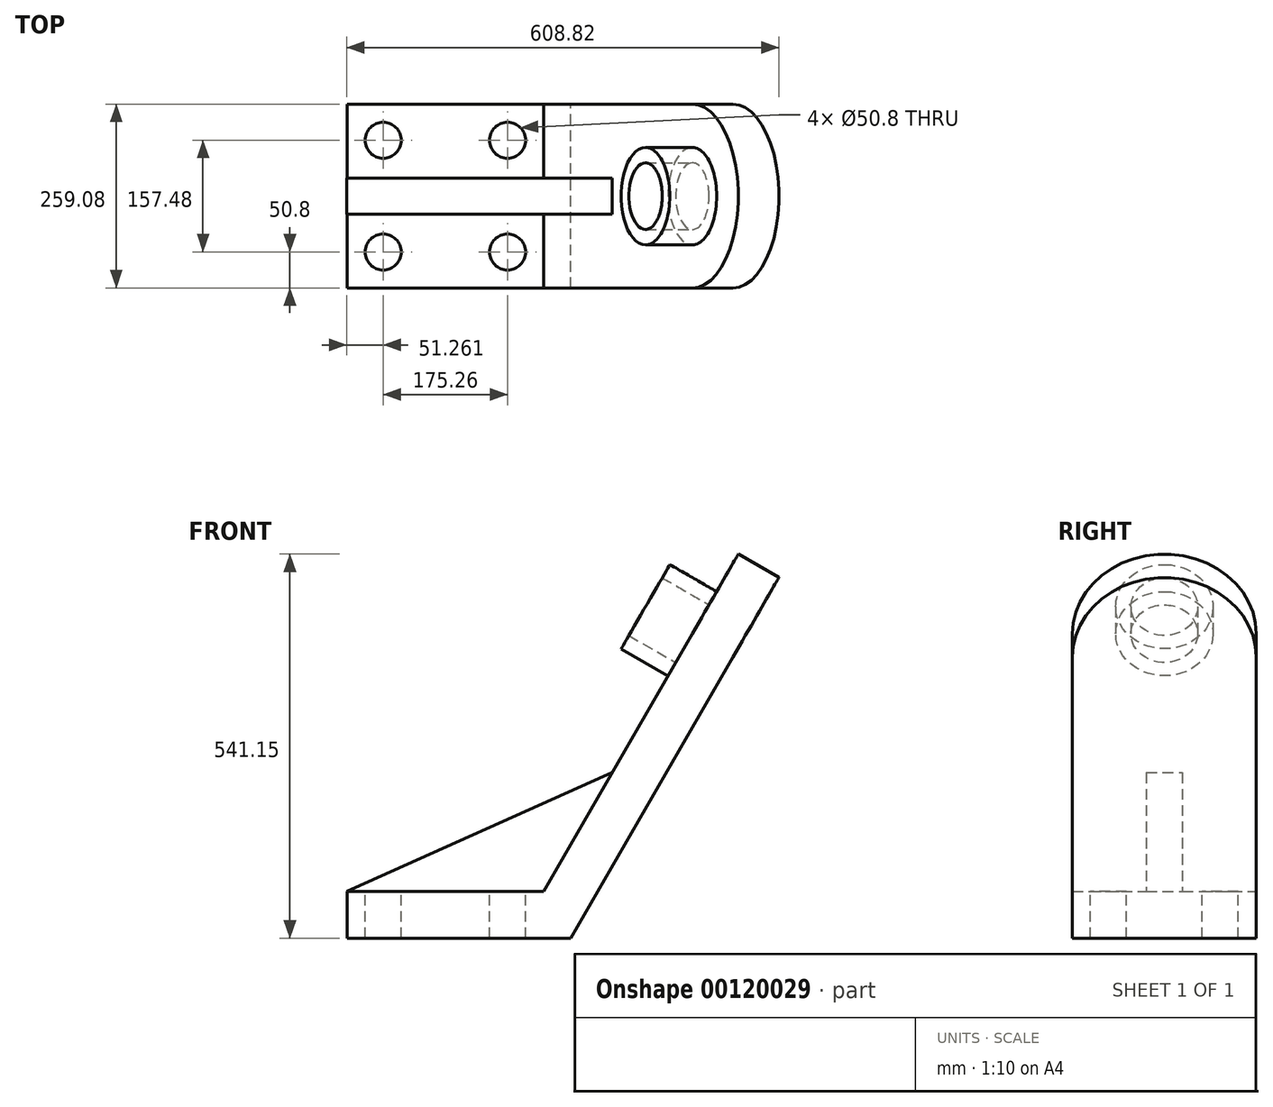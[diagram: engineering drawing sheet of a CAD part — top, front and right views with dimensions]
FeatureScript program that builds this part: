
annotation { "Feature Type Name" : "Feature", "Feature Type Description" : "" }
export const myFeature = defineFeature(function(context is Context, id is Id, definition is map)
    precondition{}
    {
        {
            var Q0;
            Q0=qCreatedBy(makeId("Front.planeOp"),FACE);
            var sketch = newSketch(context, id + "F0", { "sketchPlane" : qUnion([Q0])});
            skLineSegment(sketch, "E0", {"start": v(-237.3, 0) * mm, "end": v(39.55, 0) * mm});
            skLineSegment(sketch, "E1", {"start": v(39.55, 0) * mm, "end": v(313.86, 475.11) * mm});
            skLineSegment(sketch, "E2", {"start": v(313.86, 475.11) * mm, "end": v(371.05, 442.1) * mm});
            skLineSegment(sketch, "E3", {"start": v(371.05, 442.1) * mm, "end": v(77.68, -66.04) * mm});
            skLineSegment(sketch, "E4", {"start": v(77.68, -66.04) * mm, "end": v(-237.3, -66.04) * mm});
            skLineSegment(sketch, "E5", {"start": v(-237.3, -66.04) * mm, "end": v(-237.3, 0) * mm});
            skSolve(sketch);
        }
        {
            var Q0;
            Q0 = qSketchRegion(id + "F0", true);
            extrude(context, id + "F1", {"entities" : qUnion([Q0]), "depth" : 259.08 * mm});
        }
        {
            var Q0;
            Q0=makeQuery(id+"F1.opExtrude","SWEPT_FACE",FACE,{"disambiguationData":[OSD([sQuery(id+"F0.wireOp",EDGE,"E1")])]});
            var sketch = newSketch(context, id + "F2", { "sketchPlane" : qUnion([Q0])});
            skCircle(sketch, "E6", {"center": v(129.54, 438.85) * mm, "radius": 129.54 * mm});
            skCircle(sketch, "E7", {"center": v(129.54, 438.85) * mm, "radius": 68.58 * mm});
            skCircle(sketch, "E8", {"center": v(129.54, 438.85) * mm, "radius": 47 * mm});
            skSolve(sketch);
        }
        {
            var Q0;
            Q0=makeQuery(id+"F2.imprint","IMPRINT",FACE,{"disambiguationData":[TD([[makeQuery(id+"F2.imprint","IMPRINT",EDGE,{"derivedFrom":sQuery(id+"F2.wireOp",EDGE,"E7")}),1.0]])]});
            var Q1;
            Q1=sQuery(id+"F2.wireOp",EDGE,"E7");
            var Q2;
            Q2=sQuery(id+"F2.wireOp",EDGE,"E8");
            extrude(context, id + "F3", {"entities" : qUnion([Q0]), "operationType" : NewBodyOperationType.ADD, "surfaceEntities" : qUnion([Q1, Q2]), "depth" : 76.2 * mm});
        }
        {
            var Q0;
            Q0=makeQuery(id+"F1.opExtrude","CAP_EDGE",EDGE,{"disambiguationData":[OSD([sQuery(id+"F0.wireOp",EDGE,"E2")])],"isStart":false});
            var Q1;
            Q1=makeQuery(id+"F1.opExtrude","CAP_EDGE",EDGE,{"disambiguationData":[OSD([sQuery(id+"F0.wireOp",EDGE,"E2")])],"isStart":true});
            fillet(context, id + "F4", {"entities" : qUnion([Q0, Q1]), "radius" : 129.54 * mm, "tangentPropagation" : true, "allowEdgeOverflow" : false});
        }
        {
            var Q0;
            Q0=qCreatedBy(makeId("Front.planeOp"),FACE);
            cPlane(context, id + "F5", {"entities" : qUnion([Q0]), "cplaneType" : CPlaneType.OFFSET, "offset" : 129.54 * mm, "width" : 152.4 * mm, "height" : 152.4 * mm});
        }
        {
            var Q0;
            Q0=qCreatedBy(id+"F5.planeOp",FACE);
            var sketch = newSketch(context, id + "F6", { "sketchPlane" : qUnion([Q0])});
            skLineSegment(sketch, "E9", {"start": v(-237.77, 0) * mm, "end": v(136.07, 167.18) * mm});
            skLineSegment(sketch, "E10", {"start": v(136.07, 167.18) * mm, "end": v(39.55, 0) * mm});
            skLineSegment(sketch, "E11", {"start": v(39.55, 0) * mm, "end": v(-237.77, 0) * mm});
            skSolve(sketch);
        }
        {
            var Q0;
            Q0 = qSketchRegion(id + "F6", true);
            extrude(context, id + "F7", {"entities" : qUnion([Q0]), "operationType" : NewBodyOperationType.ADD, "endBound" : BoundingType.SYMMETRIC, "depth" : 50.8 * mm});
        }
        {
            var Q0;
            {var subQ1=sQuery(id+"F6.wireOp",EDGE,"E11");var subQ3=sQuery(id+"F0.wireOp",EDGE,"E0");Q0=makeQuery(id+"F7.boolean.opBoolean","SPLIT",FACE,{"disambiguationData":[TD([makeQuery(id+"F7.opExtrude","CAP_FACE",FACE,{"disambiguationData":[OSD([sQuery(id+"F6.wireOp",EDGE,"E9"),sQuery(id+"F6.wireOp",EDGE,"E10"),subQ1])],"isStart":true})])],"derivedFrom":makeQuery(id+"F1.opExtrude","SWEPT_FACE",FACE,{"disambiguationData":[OSD([subQ3])]})});}
            var sketch = newSketch(context, id + "F8", { "sketchPlane" : qUnion([Q0])});
            skCircle(sketch, "E12", {"center": v(-186.5, -50.8) * mm, "radius": 25.4 * mm});
            skCircle(sketch, "E13.0.1.0", {"center": v(-186.5, -208.28) * mm, "radius": 25.4 * mm});
            skCircle(sketch, "E13.1.0.0", {"center": v(-11.25, -50.8) * mm, "radius": 25.4 * mm});
            skCircle(sketch, "E13.1.1.0", {"center": v(-11.25, -208.28) * mm, "radius": 25.4 * mm});
            skLineSegment(sketch, "E13.direction1", {"start": v(-186.5, -50.8) * mm, "end": v(-11.25, -50.8) * mm, "construction": true});
            skLineSegment(sketch, "E13.direction2", {"start": v(-186.5, -50.8) * mm, "end": v(-186.5, -208.28) * mm, "construction": true});
            skSolve(sketch);
        }
        {
            var Q0;
            Q0 = qSketchRegion(id + "F8", true);
            extrude(context, id + "F9", {"entities" : qUnion([Q0]), "operationType" : NewBodyOperationType.REMOVE, "oppositeDirection" : true, "depth" : 76.2 * mm});
        }
    });
